# Revit family: Буст_ЕС_С_Eng
name_source: partatom
category: Mechanical Equipment
units: mm (PartAtom-declared; Revit-internal decimal feet)

## family parameters
Always vertical = Yes
Classification = None
Cut with Voids When Loaded = No
Part Type = Normal
Room Calculation Point = No
Round Connector Dimension = Use Diameter
Shared = No
Work Plane-Based = No

## types (16) — shared parameters
00_20_Manufacturer = Vents
00_20_Name = Inline mixed flow fan
Casing Material = Plastic, opaque, black
Frequency = 50 Hz
K = 50 mm  [stored 0.164042 ft]
Load Classification = HVAC
Maintenance zone material = <By Category>
Manufacturer = Vents
Number of Fase = 1
Temperature of moving air = -25...+55°С
URL = https://ventilation-system.com
Voltage = 230 V
zero-valued in all types: Default Elevation

## per-type parameters (varying)
- BOOST  150: A=267 mm; A1=104 mm; A2=207 mm  [stored 0.679134 ft]; Amperage=0 A; Apparent Load=46 VA; B=301 mm; B1=320 mm; C=247 mm; Clam at an angle=No; D=150 mm  [stored 0.492126 ft]; Diameter=150 mm  [stored 0.492126 ft]; Dy=145 mm  [stored 0.475722 ft]; Frame=Frame : 150; Frame_L=No; Frame_S=Yes; Handle=29 mm; Handle 1=31 mm  [stored 0.101706 ft]; Height=267 mm; Length=301 mm; Maximum Air Flow=600.0 m³/h; Power=45 W; R=75 mm  [stored 0.246063 ft]; Ry=73 mm; Sound pressure level at 3 m distance=37 dBA; Width=247 mm; X=94 mm; Z=150 mm  [stored 0.492126 ft]; a=134 mm; b=151 mm  [stored 0.495407 ft]; Сonnector vert=Yes
- BOOST  250: A=342 mm; A1=141 mm  [stored 0.462598 ft]; A2=282 mm; Amperage=1 A; Apparent Load=193 VA; B=293 mm; B1=450 mm; C=326 mm; Clam at an angle=No; D=250 mm; Diameter=250 mm; Dy=245 mm; Frame=Frame : 250; Frame_L=No; Frame_S=Yes; Handle=29 mm; Handle 1=31 mm  [stored 0.101706 ft]; Height=342 mm; Length=293 mm; Maximum Air Flow=1715.0 m³/h; Power=188 W; R=125 mm  [stored 0.410105 ft]; Ry=123 mm; Sound pressure level at 3 m distance=43 dBA; Width=326 mm; X=131 mm; Z=150 mm  [stored 0.492126 ft]; a=171 mm  [stored 0.561024 ft]; b=147 mm; Сonnector vert=Yes
- BOOST  160: A=267 mm; A1=104 mm; A2=207 mm  [stored 0.679134 ft]; Amperage=0 A; Apparent Load=46 VA; B=301 mm; B1=320 mm; C=251 mm; Clam at an angle=No; D=160 mm  [stored 0.524934 ft]; Diameter=160 mm  [stored 0.524934 ft]; Dy=155 mm  [stored 0.50853 ft]; Frame=Frame : 160; Frame_L=No; Frame_S=Yes; Handle=29 mm; Handle 1=31 mm  [stored 0.101706 ft]; Height=267 mm; Length=301 mm; Maximum Air Flow=600.0 m³/h; Power=45 W; R=80 mm  [stored 0.262467 ft]; Ry=78 mm; Sound pressure level at 3 m distance=37 dBA; Width=251 mm; X=94 mm; Z=150 mm  [stored 0.492126 ft]; a=134 mm; b=151 mm  [stored 0.495407 ft]; Сonnector vert=Yes
- BOOST  200: A=308 mm; A1=124 mm; A2=248 mm; Amperage=1 A; Apparent Load=117 VA; B=302 mm; B1=400 mm; C=293 mm; Clam at an angle=No; D=200 mm  [stored 0.656168 ft]; Diameter=200 mm  [stored 0.656168 ft]; Dy=195 mm  [stored 0.639764 ft]; Frame=Frame : 200; Frame_L=No; Frame_S=Yes; Handle=29 mm; Handle 1=31 mm  [stored 0.101706 ft]; Height=308 mm; Length=302 mm; Maximum Air Flow=1140.0 m³/h; Power=113 W; R=100 mm  [stored 0.328084 ft]; Ry=98 mm; Sound pressure level at 3 m distance=42 dBA; Width=293 mm; X=114 mm; Z=150 mm  [stored 0.492126 ft]; a=154 mm  [stored 0.505249 ft]; b=151 mm  [stored 0.495407 ft]; Сonnector vert=Yes
- BOOST  315: A=439 mm; A1=203 mm  [stored 0.66601 ft]; A2=406 mm; Amperage=1 A; Apparent Load=152 VA; B=468 mm; B1=566 mm; C=437 mm; Clam at an angle=Yes; D=310 mm; Diameter=310 mm; Dy=305 mm; Frame=Frame : 200; Frame_L=Yes; Frame_S=No; Handle=16 mm; Handle 1=18 mm  [stored 0.0590551 ft]; Height=439 mm; Length=468 mm; Maximum Air Flow=1140.0 m³/h; Power=150 W; R=155 mm  [stored 0.50853 ft]; Ry=153 mm  [stored 0.501969 ft]; Sound pressure level at 3 m distance=43 dBA; Width=566 mm; X=193 mm  [stored 0.633202 ft]; Z=300 mm; a=220 mm; b=234 mm; Сonnector vert=No
- BOOST  355: A=439 mm; A1=203 mm  [stored 0.66601 ft]; A2=406 mm; Amperage=1 A; Apparent Load=152 VA; B=372 mm; B1=566 mm; C=437 mm; Clam at an angle=Yes; D=350 mm; Diameter=350 mm; Dy=345 mm; Frame=Frame : 200; Frame_L=Yes; Frame_S=No; Handle=16 mm; Handle 1=18 mm  [stored 0.0590551 ft]; Height=439 mm; Length=372 mm; Maximum Air Flow=2485.0 m³/h; Power=150 W; R=175 mm  [stored 0.574147 ft]; Ry=173 mm; Sound pressure level at 3 m distance=43 dBA; Width=566 mm; X=193 mm  [stored 0.633202 ft]; Z=250 mm; a=220 mm; b=186 mm  [stored 0.610236 ft]; Сonnector vert=No
- BOOST  400: A=484 mm; A1=225 mm; A2=450 mm; Amperage=1 A; Apparent Load=225 VA; B=415 mm; B1=623 mm; C=482 mm; Clam at an angle=Yes; D=395 mm; Diameter=395 mm; Dy=390 mm; Frame=Frame : 200; Frame_L=Yes; Frame_S=No; Handle=16 mm; Handle 1=18 mm  [stored 0.0590551 ft]; Height=484 mm; Length=415 mm; Maximum Air Flow=3350.0 m³/h; Power=224 W; R=198 mm; Ry=195 mm  [stored 0.639764 ft]; Sound pressure level at 3 m distance=43 dBA; Width=623 mm; X=215 mm; Z=300 mm; a=242 mm; b=208 mm; Сonnector vert=No
- BOOST  150 ЕС: A=267 mm; A1=104 mm; A2=207 mm  [stored 0.679134 ft]; Amperage=0 A; Apparent Load=110 VA; B=301 mm; B1=320 mm; C=247 mm; Clam at an angle=No; D=150 mm  [stored 0.492126 ft]; Diameter=150 mm  [stored 0.492126 ft]; Dy=145 mm  [stored 0.475722 ft]; Frame=Frame : 150; Frame_L=No; Frame_S=Yes; Handle=29 mm; Handle 1=31 mm  [stored 0.101706 ft]; Height=267 mm; Length=301 mm; Maximum Air Flow=700.0 m³/h; Power=54 W; R=75 mm  [stored 0.246063 ft]; Ry=73 mm; Sound pressure level at 3 m distance=39 dBA; Width=247 mm; X=94 mm; Z=150 mm  [stored 0.492126 ft]; a=134 mm; b=151 mm  [stored 0.495407 ft]; Сonnector vert=Yes
- BOOST  160 ЕС: A=267 mm; A1=104 mm; A2=207 mm  [stored 0.679134 ft]; Amperage=0 A; Apparent Load=110 VA; B=301 mm; B1=320 mm; C=251 mm; Clam at an angle=No; D=160 mm  [stored 0.524934 ft]; Diameter=160 mm  [stored 0.524934 ft]; Dy=155 mm  [stored 0.50853 ft]; Frame=Frame : 160; Frame_L=No; Frame_S=Yes; Handle=29 mm; Handle 1=31 mm  [stored 0.101706 ft]; Height=267 mm; Length=301 mm; Maximum Air Flow=700.0 m³/h; Power=54 W; R=80 mm  [stored 0.262467 ft]; Ry=78 mm; Sound pressure level at 3 m distance=39 dBA; Width=251 mm; X=94 mm; Z=150 mm  [stored 0.492126 ft]; a=134 mm; b=151 mm  [stored 0.495407 ft]; Сonnector vert=Yes
- BOOST  200 ЕС: A=308 mm; A1=124 mm; A2=248 mm; Amperage=1 A; Apparent Load=221 VA; B=302 mm; B1=400 mm; C=293 mm; Clam at an angle=No; D=200 mm  [stored 0.656168 ft]; Diameter=200 mm  [stored 0.656168 ft]; Dy=195 mm  [stored 0.639764 ft]; Frame=Frame : 200; Frame_L=No; Frame_S=Yes; Handle=29 mm; Handle 1=31 mm  [stored 0.101706 ft]; Height=308 mm; Length=302 mm; Maximum Air Flow=1250.0 m³/h; Power=121 W; R=100 mm  [stored 0.328084 ft]; Ry=98 mm; Sound pressure level at 3 m distance=50 dBA; Width=293 mm; X=114 mm; Z=150 mm  [stored 0.492126 ft]; a=154 mm  [stored 0.505249 ft]; b=151 mm  [stored 0.495407 ft]; Сonnector vert=Yes
- BOOST  250 ЕС: A=342 mm; A1=141 mm  [stored 0.462598 ft]; A2=282 mm; Amperage=1 A; Apparent Load=308 VA; B=293 mm; B1=450 mm; C=326 mm; Clam at an angle=No; D=250 mm; Diameter=250 mm; Dy=245 mm; Frame=Frame : 250; Frame_L=No; Frame_S=Yes; Handle=29 mm; Handle 1=31 mm  [stored 0.101706 ft]; Height=342 mm; Length=293 mm; Maximum Air Flow=1800.0 m³/h; Power=168 W; R=125 mm  [stored 0.410105 ft]; Ry=123 mm; Sound pressure level at 3 m distance=49 dBA; Width=326 mm; X=131 mm; Z=150 mm  [stored 0.492126 ft]; a=171 mm  [stored 0.561024 ft]; b=147 mm; Сonnector vert=Yes
- BOOST  315 ЕС: A=439 mm; A1=203 mm  [stored 0.66601 ft]; A2=406 mm; Amperage=2 A; Apparent Load=359 VA; B=468 mm; B1=566 mm; C=437 mm; Clam at an angle=Yes; D=310 mm; Diameter=310 mm; Dy=305 mm; Frame=Frame : 200; Frame_L=Yes; Frame_S=No; Handle=16 mm; Handle 1=18 mm  [stored 0.0590551 ft]; Height=439 mm; Length=468 mm; Maximum Air Flow=3250.0 m³/h; Power=353 W; R=155 mm  [stored 0.50853 ft]; Ry=153 mm  [stored 0.501969 ft]; Sound pressure level at 3 m distance=55 dBA; Width=566 mm; X=193 mm  [stored 0.633202 ft]; Z=300 mm; a=220 mm; b=234 mm; Сonnector vert=No
- BOOST  355 ЕС: A=439 mm; A1=203 mm  [stored 0.66601 ft]; A2=406 mm; Amperage=2 A; Apparent Load=359 VA; B=372 mm; B1=566 mm; C=437 mm; Clam at an angle=Yes; D=350 mm; Diameter=350 mm; Dy=345 mm; Frame=Frame : 200; Frame_L=Yes; Frame_S=No; Handle=16 mm; Handle 1=18 mm  [stored 0.0590551 ft]; Height=439 mm; Length=372 mm; Maximum Air Flow=3685.0 m³/h; Power=353 W; R=175 mm  [stored 0.574147 ft]; Ry=173 mm; Sound pressure level at 3 m distance=55 dBA; Width=566 mm; X=193 mm  [stored 0.633202 ft]; Z=250 mm; a=220 mm; b=186 mm  [stored 0.610236 ft]; Сonnector vert=No
- BOOST  400 ЕС: A=484 mm; A1=225 mm; A2=450 mm; Amperage=5 A; Apparent Load=1104 VA; B=415 mm; B1=623 mm; C=482 mm; Clam at an angle=Yes; D=395 mm; Diameter=395 mm; Dy=390 mm; Frame=Frame : 200; Frame_L=Yes; Frame_S=No; Handle=16 mm; Handle 1=18 mm  [stored 0.0590551 ft]; Height=484 mm; Length=415 mm; Maximum Air Flow=5700.0 m³/h; Power=726 W; R=198 mm; Ry=195 mm  [stored 0.639764 ft]; Sound pressure level at 3 m distance=60 dBA; Width=623 mm; X=215 mm; Z=300 mm; a=242 mm; b=208 mm; Сonnector vert=No
- BOOST  315 ЕС С: A=439 mm; A1=203 mm  [stored 0.66601 ft]; A2=406 mm; Amperage=2 A; Apparent Load=359 VA; B=468 mm; B1=566 mm; C=437 mm; Clam at an angle=Yes; D=310 mm; Diameter=310 mm; Dy=305 mm; Frame=Frame : 200; Frame_L=Yes; Frame_S=No; Handle=16 mm; Handle 1=18 mm  [stored 0.0590551 ft]; Height=439 mm; Length=468 mm; Maximum Air Flow=3250.0 m³/h; Power=353 W; R=155 mm  [stored 0.50853 ft]; Ry=153 mm  [stored 0.501969 ft]; Sound pressure level at 3 m distance=55 dBA; Width=566 mm; X=193 mm  [stored 0.633202 ft]; Z=300 mm; a=220 mm; b=234 mm; Сonnector vert=No
- BOOST  355 ЕС С: A=439 mm; A1=203 mm  [stored 0.66601 ft]; A2=406 mm; Amperage=3 A; Apparent Load=713 VA; B=372 mm; B1=566 mm; C=437 mm; Clam at an angle=Yes; D=350 mm; Diameter=350 mm; Dy=345 mm; Frame=Frame : 200; Frame_L=Yes; Frame_S=No; Handle=16 mm; Handle 1=18 mm  [stored 0.0590551 ft]; Height=439 mm; Length=372 mm; Maximum Air Flow=4630.0 m³/h; Power=701 W; R=175 mm  [stored 0.574147 ft]; Ry=173 mm; Sound pressure level at 3 m distance=60 dBA; Width=566 mm; X=193 mm  [stored 0.633202 ft]; Z=250 mm; a=220 mm; b=186 mm  [stored 0.610236 ft]; Сonnector vert=No

note: column(s) folded — value = type name in every type: 00_20_Type

note: [stored X ft] marks values corroborated as IEEE doubles in the binary element streams (Revit-internal decimal feet)
